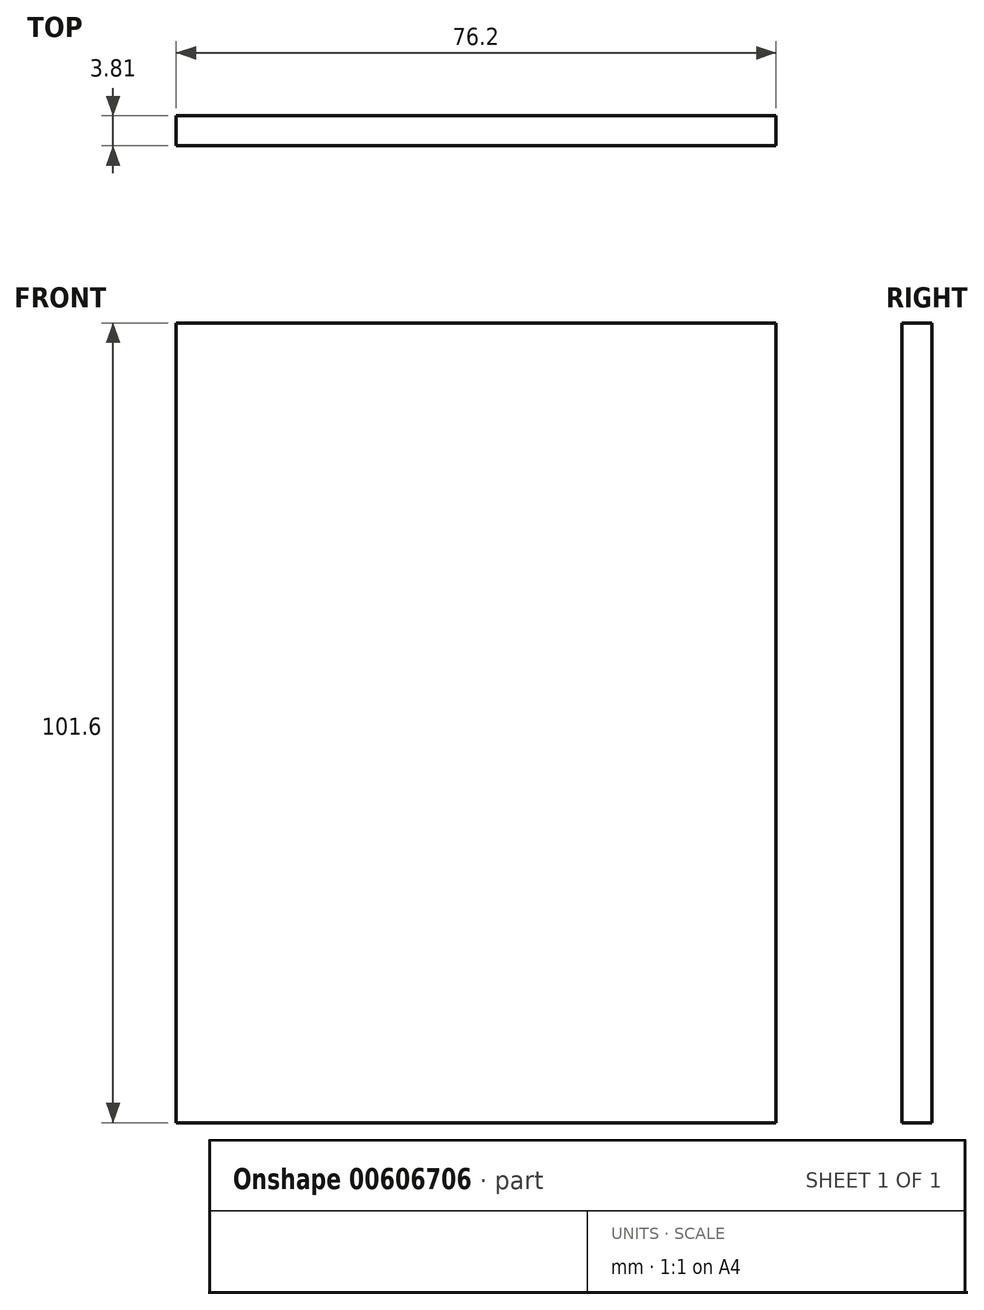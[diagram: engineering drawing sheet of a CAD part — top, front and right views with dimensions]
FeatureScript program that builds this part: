
annotation { "Feature Type Name" : "Feature", "Feature Type Description" : "" }
export const myFeature = defineFeature(function(context is Context, id is Id, definition is map)
    precondition{}
    {
        {
            var Q0;
            Q0=qCreatedBy(makeId("Front.planeOp"),FACE);
            var sketch = newSketch(context, id + "F0", { "sketchPlane" : qUnion([Q0])});
            skLineSegment(sketch, "E0.bottom", {"start": v(-39.52, 50.94) * mm, "end": v(36.68, 50.94) * mm});
            skLineSegment(sketch, "E0.top", {"start": v(-39.52, -50.66) * mm, "end": v(36.68, -50.66) * mm});
            skLineSegment(sketch, "E0.left", {"start": v(-39.52, 50.94) * mm, "end": v(-39.52, -50.66) * mm});
            skLineSegment(sketch, "E0.right", {"start": v(36.68, 50.94) * mm, "end": v(36.68, -50.66) * mm});
            skSolve(sketch);
        }
        {
            var Q0;
            Q0=makeQuery(id+"F0.imprint","IMPRINT",FACE,{"disambiguationData":[TD([[makeQuery(id+"F0.imprint","IMPRINT",EDGE,{"derivedFrom":sQuery(id+"F0.wireOp",EDGE,"E0.bottom")}),-1.0]])]});
            extrude(context, id + "F1", {"entities" : qUnion([Q0]), "depth" : 3.8 * mm, "offsetDistance" : 25.4 * mm});
        }
    });
